# Revit family: 795280001_Griferia Marruecos a Pared Pico S
name_source: partatom
category: Plumbing Fixtures
units: mm (PartAtom-declared; Revit-internal decimal feet)

## family parameters
Always vertical = Yes
Cut with Voids When Loaded = No
Host = Wall
OmniClass Number = 23.31.11.00
OmniClass Title = Faucets
Part Type = Normal
Room Calculation Point = No
Round Connector Dimension = Use Diameter
Shared = No

## types (1)
- Type 1
    Alto = 202 mm  [stored 0.66273 ft]
    Ancho = 63 mm  [stored 0.206693 ft]
    Capacidad de flujo máximo por norma = 9,5 L/min.
    Ciclo de vida de la unidad de cierre = 250.000 ciclos.
    Creado por = BIMBAU
    Cuidado Y Limpieza = Los acabados superﬁciales son aquellos que le imprimen una apariencia
especial y estética a su producto y además le brindan protección. Para
prolongar sus cualidades es vital que la limpieza profunda del producto se
haga únicamente con agua y jabón suave y que en el secado y el brillo se
utilice un paño de algodón limpio; dicha limpieza se recomienda 2 veces a
la semana y en zonas costeras a diario por la salinidad del ambiente. Por
ningún motivo deben usarse elementos abrasivos, ácidos o disolventes
para la limpieza del producto. Los acabados pueden variar su
comportamiento en zonas costeras y/o en ambientes corrosivos
    Default Elevation = 0 mm  [stored 0 ft]
    Description = El lavaplatos de paraed en S Marruecos ha sido diseñada para trabajar en perfecta
armonía con el espacio; inspirada en las necesidades del consumidor latinoamericano
dando como resultado un producto robusto y funcional. Su pico giratorio le permite al
usuario tomar ventaja del área del lavaplatos. Ideal para instalaciones donde no se
necesita mezclar agua fría y caliente y donde la grifería vaya empotrada a la pared.
Incorpora un sistema aireador que genera un chorro de agua espumoso,
agradable al tacto. Grifería de lavaplatos con ahorro de agua. Acabado superior, mayor espesor en el cromado que lo hace más brillante y resistente a la corrosión. Pico oscilante que permite mayor alcance y mas comodidad dando confort en el uso. Fácil limpieza: Diseño que evita la acumulación de impurezas.
    Fecha de creación = 5/11/2021
    Garantía = 30 Años
    Manufacturer = Corona - Grival
    Material = Corona_Plastico_Cromado
    Model = Griferia Lavaplatos de Pared en S Marruecos
    Peso Bruto aprox = 540gr. / 1,19Lb.
    Peso Neto aprox = 480gr. / 1,06Lb.
    Presión máxima recomendada = 125 psi.
    Presión mínima recomendada = 20 psi.
    Profundidad = 250 mm  [stored 0.82021 ft]
    Recubrimientos = Resistente a la corrosión, pelado y decoloración por agua. Recubrimientos no tóxicos
    Referencia = 795280001
    Temperaturas máxima de trabajo = 71 ºC / 159,8 ºF.
    Temperaturas mínima de trabajo = 5 ºC / 41 ºF.
    Uso = Doméstico
    Vida útil = 50.000 ciclos.

note: [stored X ft] marks values corroborated as IEEE doubles in the binary element streams (Revit-internal decimal feet)

## geometry (parser evidence)
native form markers: Sweep x7
no freeform markers — native parametric forms only
